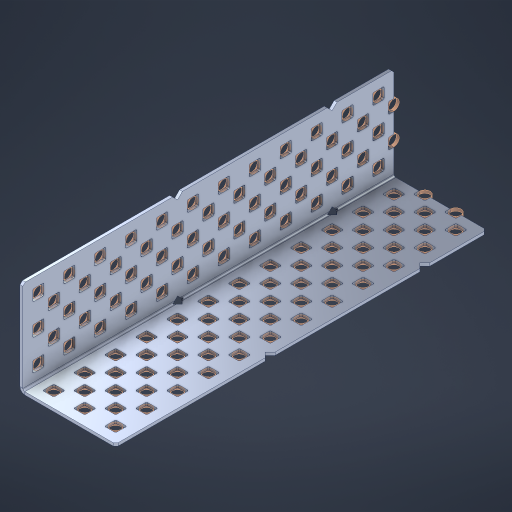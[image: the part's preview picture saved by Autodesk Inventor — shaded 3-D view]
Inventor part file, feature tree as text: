
AUTODESK INVENTOR PART (.ipt)
format: ipt  version: 2023 (Build 270158000, 158)  size: 1,501,696 bytes
history: native  units: in
note: dims shown in document units (in); Inventor stores cm internally (conversion verified against a paired STEP export)
features: other x126, extrude x118, sheet_metal_op x8, sketch x7, pattern_linear x3, mirror x1, chamfer x1
ambient origin geometry x8: Origin, YZ Plane, XZ Plane, XY Plane, X Axis, Y Axis, Z Axis, Center Point
bodies: Solid1 (feature_tree), Body (feature_tree)
feature tree (264):
  sheet_metal_op  "Flanges"
  sheet_metal_op  "Body Pattern"
  pattern_linear  "Center Double"  Spacing1=1.5in  [1 undecoded]
  pattern_linear  "Center Pattern"  Spacing1=0.1875in  [1 undecoded]
  other  "Arc Length"
  pattern_linear  "Notch Pattern"  Spacing1=0.0469in  [1 undecoded]
  other  "Diagonal Plane"
  mirror  "Everything Mirrored"
  chamfer  "End Chamfer"
  sketch  "Sketch1"  dims[d0=1.5in]
  other  "Plate1"
  sketch  "Sketch2"  dims[d1=6.0in]
  other  "Plate2"
  sheet_metal_op  "Bend1"
  sheet_metal_op  "Corner1"
  sketch  "Sketch8"  dims[d2=0.0469in]
  sketch  "Sketch9"  dims[d3=0.0469in]
  other  "Srf91"
  sheet_metal_op  "Body Pattern Sketch"
  other  "Srf92"
  sketch  "Sketch13"  dims[d4=0.0234in]
  sketch  "Sketch15"  dims[d5=0.0938in]
  sketch  "Sketch16"  dims[d6=0.0469in d7=1.5in d8=90.0deg d9=0.0312in d10=0.1875in d11=0.0469in d12=0.0469in d49=0.182in d50=0.02in d52=0.25in d53=0.0469in d54=0.0in d55=0.172in d56=1.0in d57=0.0in d85=0.1473in d86=0.1659in d89=0.0469in d90=0.0in d91=0.04in d92=0.0491in d95=2.5in d96=0.04in d97=0.25in d98=45.0deg d106=0.182in d107=0.02in d110=0.0469in d111=0.0in d112=0.172in d113=0.5in d114=0.0in d117=0.5in d126=0.0491in d127=0.1227in d128=0.08in d129=0.04in d130=2.5in d131=0.25in d132=4.7244in d134=0.5in d135=1.1811in d137=0.5in d140=0.5in d141=1.0in d142=0.3937in d144=0.5in d145=0.071in d146=0.7874in d148=0.5in]
  other  "Srf786"
  other  "Srf856"
  other  "Srf889"
  other  "Srf890"
  other  "Srf891"
  other  "Srf1275"
  other  "Srf1276"
  other  "Srf1278"
  other  "Srf1277"
  other  "Srf1285"
  other  "Srf1286"
  other  "Srf1287"
  other  "Srf1445"
  other  "Srf1446"
  other  "Srf1447"
  other  "Srf1448"
  other  "Srf1449"
  other  "Srf1537"
  other  "Srf1538"
  other  "Srf1539"
  other  "Srf1540"
  other  "Srf1541"
  other  "Srf1807"
  other  "Srf1808"
  other  "Srf1809"
  other  "Srf1959"
  other  "Srf1960"
  other  "Srf1961"
  other  "Srf2009"
  other  "Srf2010"
  other  "Srf2011"
  other  "Srf2012"
  other  "Srf2013"
  other  "Srf2014"
  other  "Srf2015"
  other  "Srf2016"
  other  "Srf2017"
  other  "Srf2018"
  other  "Srf2019"
  other  "Srf2020"
  other  "Srf2043"
  other  "Srf2044"
  other  "Srf2045"
  other  "Srf2046"
  other  "Srf2047"
  other  "Srf2048"
  other  "Srf2049"
  other  "Srf2050"
  other  "Srf2051"
  other  "Srf2052"
  other  "Srf2053"
  other  "Srf2076"
  other  "Srf2077"
  other  "Srf2078"
  other  "Srf2079"
  other  "Srf2080"
  other  "Srf2081"
  other  "Srf2082"
  other  "Srf2083"
  other  "Srf2084"
  other  "Srf2085"
  other  "Srf2086"
  other  "Srf2087"
  other  "Srf2088"
  other  "Srf2089"
  other  "Srf2090"
  other  "Srf2091"
  other  "Srf2092"
  other  "Srf2093"
  other  "Srf2094"
  other  "Srf2095"
  other  "Srf2096"
  other  "Srf2097"
  other  "Srf2098"
  other  "Srf2099"
  other  "Srf2100"
  other  "Srf2101"
  other  "Srf2102"
  other  "Srf2103"
  other  "Srf2104"
  other  "Srf2105"
  other  "Srf2106"
  other  "Srf2107"
  other  "Srf2108"
  other  "Srf2109"
  other  "Srf2179"
  other  "Srf2180"
  other  "Srf2181"
  other  "Srf2182"
  other  "Srf2183"
  other  "Srf2184"
  other  "Srf2185"
  other  "Srf2186"
  other  "Srf2187"
  other  "Srf2188"
  other  "Srf2189"
  other  "Srf2190"
  other  "Srf2191"
  other  "Srf2192"
  other  "Srf2193"
  other  "Srf2194"
  other  "Srf2195"
  other  "Srf2196"
  other  "Srf2197"
  other  "Srf2198"
  other  "Srf2199"
  other  "Srf2200"
  other  "Srf2201"
  other  "Srf2202"
  other  "Srf2203"
  other  "Srf2204"
  other  "Srf2205"
  other  "Srf2206"
  other  "Srf2207"
  other  "Srf2208"
  other  "Srf2209"
  other  "Srf2210"
  other  "Srf2211"
  sheet_metal_op  "Body Stamp"
  sheet_metal_op  "Body Circle"
  other  "Center Stamp"
  other  "Center Circle"
  sheet_metal_op  "Notch"
  extrude  "ExtrusionSrf92"  Depth=0.0469in
  extrude  "ExtrusionSrf856"  Depth=0.182in
  extrude  "ExtrusionSrf889"  Depth=0.02in
  extrude  "ExtrusionSrf890"  Depth=0.25in
  extrude  "ExtrusionSrf891"  Depth=0.0469in
  extrude  "ExtrusionSrf1275"  TaperAngle=0.0deg  [1 undecoded]
  extrude  "ExtrusionSrf1276"  Depth=0.5in
  extrude  "ExtrusionSrf1277"  Depth=1.0in TaperAngle=0.0deg
  extrude  "ExtrusionSrf1345"  Depth=0.5in
  extrude  "ExtrusionSrf1346"  Depth=0.5in
  extrude  "ExtrusionSrf1347"  Depth=0.0469in
  extrude  "ExtrusionSrf1348"  Depth=0.5in TaperAngle=0.0deg
  extrude  "ExtrusionSrf1445"  Depth=0.5in
  extrude  "ExtrusionSrf1446"  Depth=0.25in TaperAngle=45.0deg
  extrude  "ExtrusionSrf1447"  Depth=0.182in
  extrude  "ExtrusionSrf1448"  Depth=0.02in
  extrude  "ExtrusionSrf1449"  Depth=0.0469in
  extrude  "ExtrusionSrf1537"  TaperAngle=0.0deg  [1 undecoded]
  extrude  "ExtrusionSrf1538"  Depth=0.5in
  extrude  "ExtrusionSrf1539"  Depth=0.5in TaperAngle=0.0deg
  extrude  "ExtrusionSrf1540"  Depth=0.5in
  extrude  "ExtrusionSrf1541"  Depth=0.5in
  extrude  "ExtrusionSrf1807"  Depth=0.5in
  extrude  "ExtrusionSrf1808"  Depth=0.5in
  extrude  "ExtrusionSrf1809"  Depth=0.5in
  extrude  "ExtrusionSrf1959"  Depth=0.5in
  extrude  "ExtrusionSrf1960"  Depth=0.25in
  extrude  "ExtrusionSrf1961"  Depth=0.5in
  extrude  "ExtrusionSrf2009"  Depth=0.5in
  extrude  "ExtrusionSrf2010"  Depth=0.5in
  extrude  "ExtrusionSrf2011"  Depth=1.0in
  extrude  "ExtrusionSrf2012"  Depth=0.3937in
  extrude  "ExtrusionSrf2013"  Depth=0.5in
  extrude  "ExtrusionSrf2014"  Depth=0.5in
  extrude  "ExtrusionSrf2015"  [1 undecoded]
  extrude  "ExtrusionSrf2016"  [1 undecoded]
  extrude  "ExtrusionSrf2017"  [1 undecoded]
  extrude  "ExtrusionSrf2018"  [1 undecoded]
  extrude  "ExtrusionSrf2019"  [1 undecoded]
  extrude  "ExtrusionSrf2020"  [1 undecoded]
  extrude  "ExtrusionSrf2043"  [1 undecoded]
  extrude  "ExtrusionSrf2044"  [1 undecoded]
  extrude  "ExtrusionSrf2045"  [1 undecoded]
  extrude  "ExtrusionSrf2046"  [1 undecoded]
  extrude  "ExtrusionSrf2047"  [1 undecoded]
  extrude  "ExtrusionSrf2048"  [1 undecoded]
  extrude  "ExtrusionSrf2049"  [1 undecoded]
  extrude  "ExtrusionSrf2050"  [1 undecoded]
  extrude  "ExtrusionSrf2051"  [1 undecoded]
  extrude  "ExtrusionSrf2052"  [1 undecoded]
  extrude  "ExtrusionSrf2053"  [1 undecoded]
  extrude  "ExtrusionSrf2076"  [1 undecoded]
  extrude  "ExtrusionSrf2077"  [1 undecoded]
  extrude  "ExtrusionSrf2078"  [1 undecoded]
  extrude  "ExtrusionSrf2079"  [1 undecoded]
  extrude  "ExtrusionSrf2080"  [1 undecoded]
  extrude  "ExtrusionSrf2081"  [1 undecoded]
  extrude  "ExtrusionSrf2082"  [1 undecoded]
  extrude  "ExtrusionSrf2083"  [1 undecoded]
  extrude  "ExtrusionSrf2084"  [1 undecoded]
  extrude  "ExtrusionSrf2085"  [1 undecoded]
  extrude  "ExtrusionSrf2086"  [1 undecoded]
  extrude  "ExtrusionSrf2087"  [1 undecoded]
  extrude  "ExtrusionSrf2088"  [1 undecoded]
  extrude  "ExtrusionSrf2089"  [1 undecoded]
  extrude  "ExtrusionSrf2090"  [1 undecoded]
  extrude  "ExtrusionSrf2091"  [1 undecoded]
  extrude  "ExtrusionSrf2092"  [1 undecoded]
  extrude  "ExtrusionSrf2093"  [1 undecoded]
  extrude  "ExtrusionSrf2094"  [1 undecoded]
  extrude  "ExtrusionSrf2095"  [1 undecoded]
  extrude  "ExtrusionSrf2096"  [1 undecoded]
  extrude  "ExtrusionSrf2097"  [1 undecoded]
  extrude  "ExtrusionSrf2098"  [1 undecoded]
  extrude  "ExtrusionSrf2099"  [1 undecoded]
  extrude  "ExtrusionSrf2100"  [1 undecoded]
  extrude  "ExtrusionSrf2101"  [1 undecoded]
  extrude  "ExtrusionSrf2102"  [1 undecoded]
  extrude  "ExtrusionSrf2103"  [1 undecoded]
  extrude  "ExtrusionSrf2104"  [1 undecoded]
  extrude  "ExtrusionSrf2105"  [1 undecoded]
  extrude  "ExtrusionSrf2106"  [1 undecoded]
  extrude  "ExtrusionSrf2107"  [1 undecoded]
  extrude  "ExtrusionSrf2108"  [1 undecoded]
  extrude  "ExtrusionSrf2109"  [1 undecoded]
  extrude  "ExtrusionSrf2179"  [1 undecoded]
  extrude  "ExtrusionSrf2180"  [1 undecoded]
  extrude  "ExtrusionSrf2181"  [1 undecoded]
  extrude  "ExtrusionSrf2182"  [1 undecoded]
  extrude  "ExtrusionSrf2183"  [1 undecoded]
  extrude  "ExtrusionSrf2184"  [1 undecoded]
  extrude  "ExtrusionSrf2185"  [1 undecoded]
  extrude  "ExtrusionSrf2186"  [1 undecoded]
  extrude  "ExtrusionSrf2187"  [1 undecoded]
  extrude  "ExtrusionSrf2188"  [1 undecoded]
  extrude  "ExtrusionSrf2189"  [1 undecoded]
  extrude  "ExtrusionSrf2190"  [1 undecoded]
  extrude  "ExtrusionSrf2191"  [1 undecoded]
  extrude  "ExtrusionSrf2192"  [1 undecoded]
  extrude  "ExtrusionSrf2193"  [1 undecoded]
  extrude  "ExtrusionSrf2194"  [1 undecoded]
  extrude  "ExtrusionSrf2195"  [1 undecoded]
  extrude  "ExtrusionSrf2196"  [1 undecoded]
  extrude  "ExtrusionSrf2197"  [1 undecoded]
  extrude  "ExtrusionSrf2198"  [1 undecoded]
  extrude  "ExtrusionSrf2199"  [1 undecoded]
  extrude  "ExtrusionSrf2200"  [1 undecoded]
  extrude  "ExtrusionSrf2201"  [1 undecoded]
  extrude  "ExtrusionSrf2202"  [1 undecoded]
  extrude  "ExtrusionSrf2203"  [1 undecoded]
  extrude  "ExtrusionSrf2204"  [1 undecoded]
  extrude  "ExtrusionSrf2205"  [1 undecoded]
  extrude  "ExtrusionSrf2206"  [1 undecoded]
  extrude  "ExtrusionSrf2207"  [1 undecoded]
  extrude  "ExtrusionSrf2208"  [1 undecoded]
  extrude  "ExtrusionSrf2209"  [1 undecoded]
  extrude  "ExtrusionSrf2210"  [1 undecoded]
  extrude  "ExtrusionSrf2211"  [1 undecoded]
note: 89 required parameter values undecoded (feature->parameter linkage not recoverable at this tier; creation-order binding heuristic only, values carry confidence <= 0.55)
